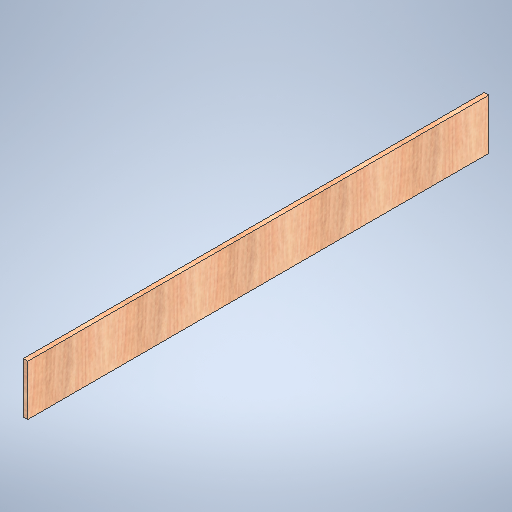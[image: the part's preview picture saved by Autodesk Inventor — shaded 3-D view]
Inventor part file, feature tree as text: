
AUTODESK INVENTOR PART (.ipt)
format: ipt  version: 2025.1 (Build 291241020, 241B)  size: 319,488 bytes
history: native  units: in
note: dims shown in document units (in); Inventor stores cm internally (conversion verified against a paired STEP export)
features: extrude x1, sketch x1
ambient origin geometry x8: Origin, YZ Plane, XZ Plane, XY Plane, X Axis, Y Axis, Z Axis, Center Point
bodies: Solid1 (feature_tree)
feature tree (2):
  extrude  "Extrusion1"  Depth=0.5in TaperAngle=0.0deg
  sketch  "Sketch1"  dims[d1=50.25in d2=0.5in d3=0.0in d4=5.5in]
